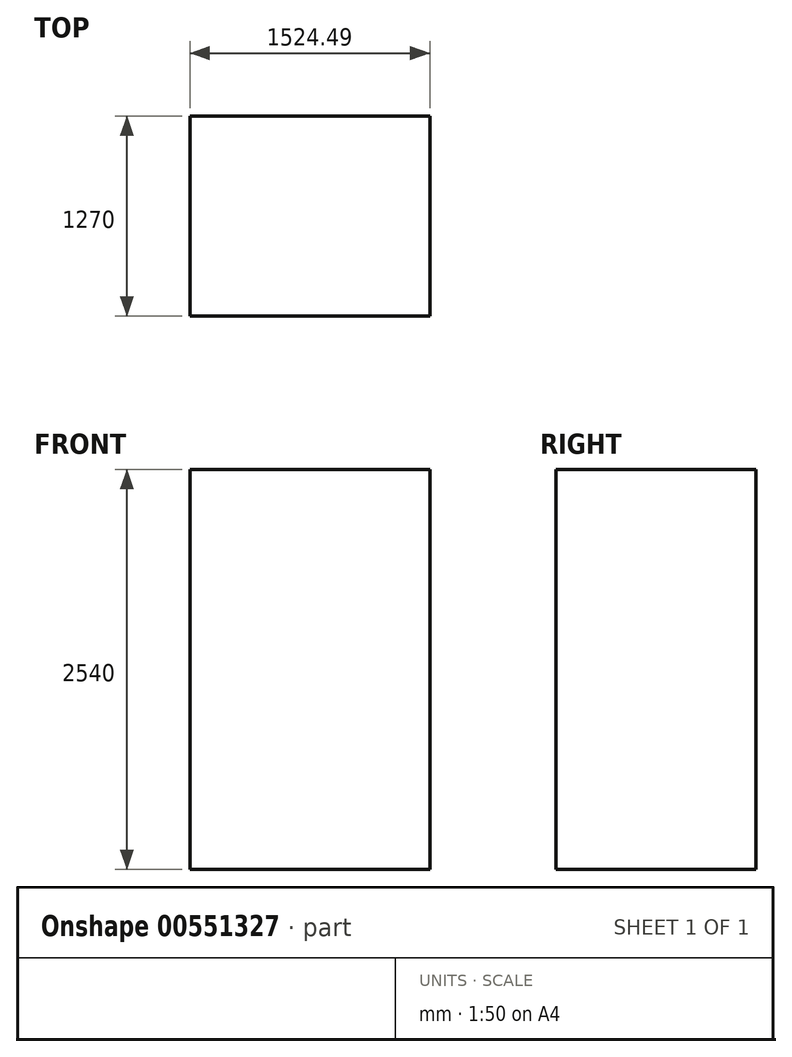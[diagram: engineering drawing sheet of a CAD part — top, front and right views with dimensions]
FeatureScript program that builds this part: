
annotation { "Feature Type Name" : "Feature", "Feature Type Description" : "" }
export const myFeature = defineFeature(function(context is Context, id is Id, definition is map)
    precondition{}
    {
        {
            var Q0;
            Q0=qCreatedBy(makeId("Top.planeOp"),FACE);
            var sketch = newSketch(context, id + "F0", { "sketchPlane" : qUnion([Q0])});
            skLineSegment(sketch, "E0.bottom", {"start": v(-766.94, 609) * mm, "end": v(757.55, 609) * mm});
            skLineSegment(sketch, "E0.top", {"start": v(-766.94, -661) * mm, "end": v(757.55, -661) * mm});
            skLineSegment(sketch, "E0.left", {"start": v(-766.94, 609) * mm, "end": v(-766.94, -661) * mm});
            skLineSegment(sketch, "E0.right", {"start": v(757.55, 609) * mm, "end": v(757.55, -661) * mm});
            skSolve(sketch);
        }
        {
            var Q0;
            Q0=makeQuery(id+"F0.imprint","IMPRINT",FACE,{"disambiguationData":[TD([[makeQuery(id+"F0.imprint","IMPRINT",EDGE,{"derivedFrom":sQuery(id+"F0.wireOp",EDGE,"E0.bottom")}),-1.0]])]});
            extrude(context, id + "F1", {"entities" : qUnion([Q0]), "depth" : 2540 * mm, "offsetDistance" : 25.4 * mm});
        }
    });
